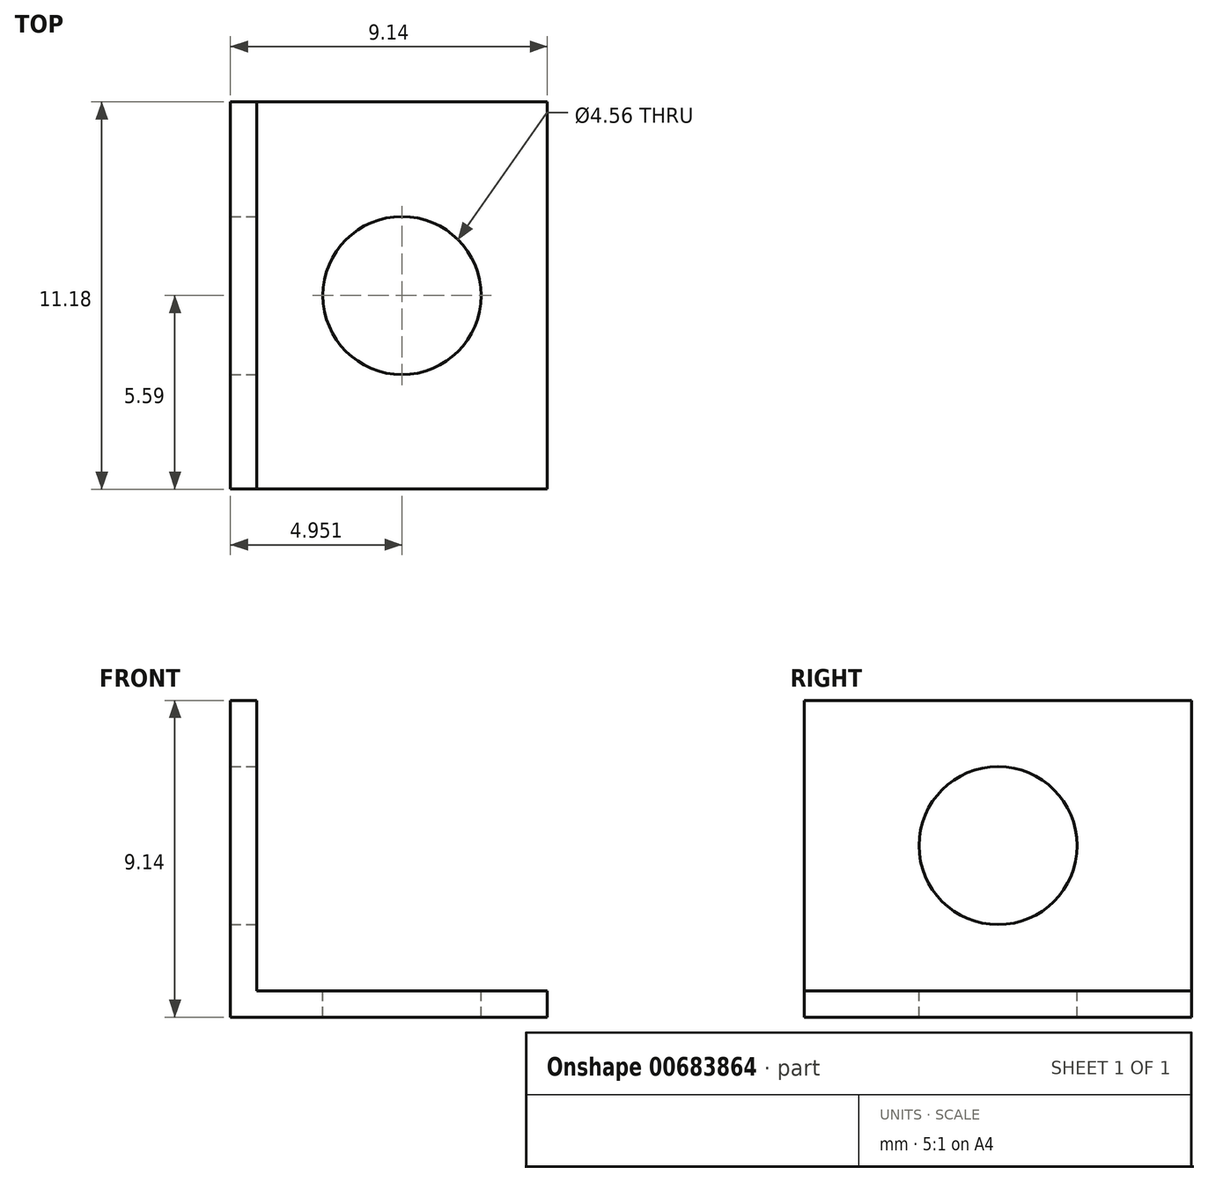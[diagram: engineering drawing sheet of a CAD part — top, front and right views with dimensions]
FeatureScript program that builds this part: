
annotation { "Feature Type Name" : "Feature", "Feature Type Description" : "" }
export const myFeature = defineFeature(function(context is Context, id is Id, definition is map)
    precondition{}
    {
        {
            var Q0;
            Q0=qCreatedBy(makeId("Front.planeOp"),FACE);
            var sketch = newSketch(context, id + "F0", { "sketchPlane" : qUnion([Q0])});
            skLineSegment(sketch, "E0.bottom", {"start": v(4.57, -4.57) * mm, "end": v(-4.57, -4.57) * mm});
            skLineSegment(sketch, "E0.top", {"start": v(4.57, 4.57) * mm, "end": v(-4.57, 4.57) * mm});
            skLineSegment(sketch, "E0.left", {"start": v(4.57, -4.57) * mm, "end": v(4.57, 4.57) * mm});
            skLineSegment(sketch, "E0.right", {"start": v(-4.57, -4.57) * mm, "end": v(-4.57, 4.57) * mm});
            skPoint(sketch, "E0.middle", {"position": v(0, 0) * mm});
            skSolve(sketch);
        }
        {
            var Q0;
            Q0 = qSketchRegion(id + "F0", true);
            extrude(context, id + "F1", {"entities" : qUnion([Q0]), "depth" : 5.6 * mm, "offsetDistance" : 25.4 * mm, "hasSecondDirection" : true, "secondDirectionOppositeDirection" : true, "secondDirectionDepth" : 5.6 * mm});
        }
        {
            var Q0;
            Q0=makeQuery(id+"F1.opExtrude","SWEPT_FACE",FACE,{"disambiguationData":[OSD([sQuery(id+"F0.wireOp",EDGE,"E0.top")])]});
            var Q1;
            Q1=makeQuery(id+"F1.opExtrude","SWEPT_FACE",FACE,{"disambiguationData":[OSD([sQuery(id+"F0.wireOp",EDGE,"E0.left")])]});
            var Q2;
            Q2=makeQuery(id+"F1.opExtrude","CAP_FACE",FACE,{"disambiguationData":[OSD([sQuery(id+"F0.wireOp",EDGE,"E0.bottom"),sQuery(id+"F0.wireOp",EDGE,"E0.top"),sQuery(id+"F0.wireOp",EDGE,"E0.left"),sQuery(id+"F0.wireOp",EDGE,"E0.right")])],"isStart":false});
            var Q3;
            Q3=makeQuery(id+"F1.opExtrude","CAP_FACE",FACE,{"disambiguationData":[OSD([sQuery(id+"F0.wireOp",EDGE,"E0.bottom"),sQuery(id+"F0.wireOp",EDGE,"E0.top"),sQuery(id+"F0.wireOp",EDGE,"E0.left"),sQuery(id+"F0.wireOp",EDGE,"E0.right")])],"isStart":true});
            shell(context, id + "F2", {"entities" : qUnion([Q0, Q1, Q2, Q3]), "thickness" : 0.76 * mm});
        }
        {
            var Q0;
            Q0=makeQuery(id+"F2.opShell","OFFSET_FACE",FACE,{"disambiguationData":[OSD([sQuery(id+"F0.wireOp",EDGE,"E0.right")])]});
            var sketch = newSketch(context, id + "F3", { "sketchPlane" : qUnion([Q0])});
            skCircle(sketch, "E1", {"center": v(0, 0.38) * mm, "radius": 2.28 * mm});
            skSolve(sketch);
        }
        {
            var Q0;
            Q0 = qSketchRegion(id + "F3", true);
            extrude(context, id + "F4", {"entities" : qUnion([Q0]), "operationType" : NewBodyOperationType.REMOVE, "oppositeDirection" : true, "depth" : 0.76 * mm, "offsetDistance" : 25.4 * mm});
        }
        {
            var Q0;
            Q0=makeQuery(id+"F2.opShell","OFFSET_FACE",FACE,{"disambiguationData":[OSD([sQuery(id+"F0.wireOp",EDGE,"E0.bottom")])]});
            var sketch = newSketch(context, id + "F5", { "sketchPlane" : qUnion([Q0])});
            skCircle(sketch, "E2", {"center": v(0.38, 0) * mm, "radius": 2.28 * mm});
            skSolve(sketch);
        }
        {
            var Q0;
            Q0=makeQuery(id+"F5.imprint","IMPRINT",FACE,{"disambiguationData":[TD([[makeQuery(id+"F5.imprint","IMPRINT",EDGE,{"derivedFrom":sQuery(id+"F5.wireOp",EDGE,"E2")}),1.0]])]});
            extrude(context, id + "F6", {"entities" : qUnion([Q0]), "operationType" : NewBodyOperationType.REMOVE, "oppositeDirection" : true, "depth" : 0.76 * mm, "offsetDistance" : 25.4 * mm});
        }
    });
